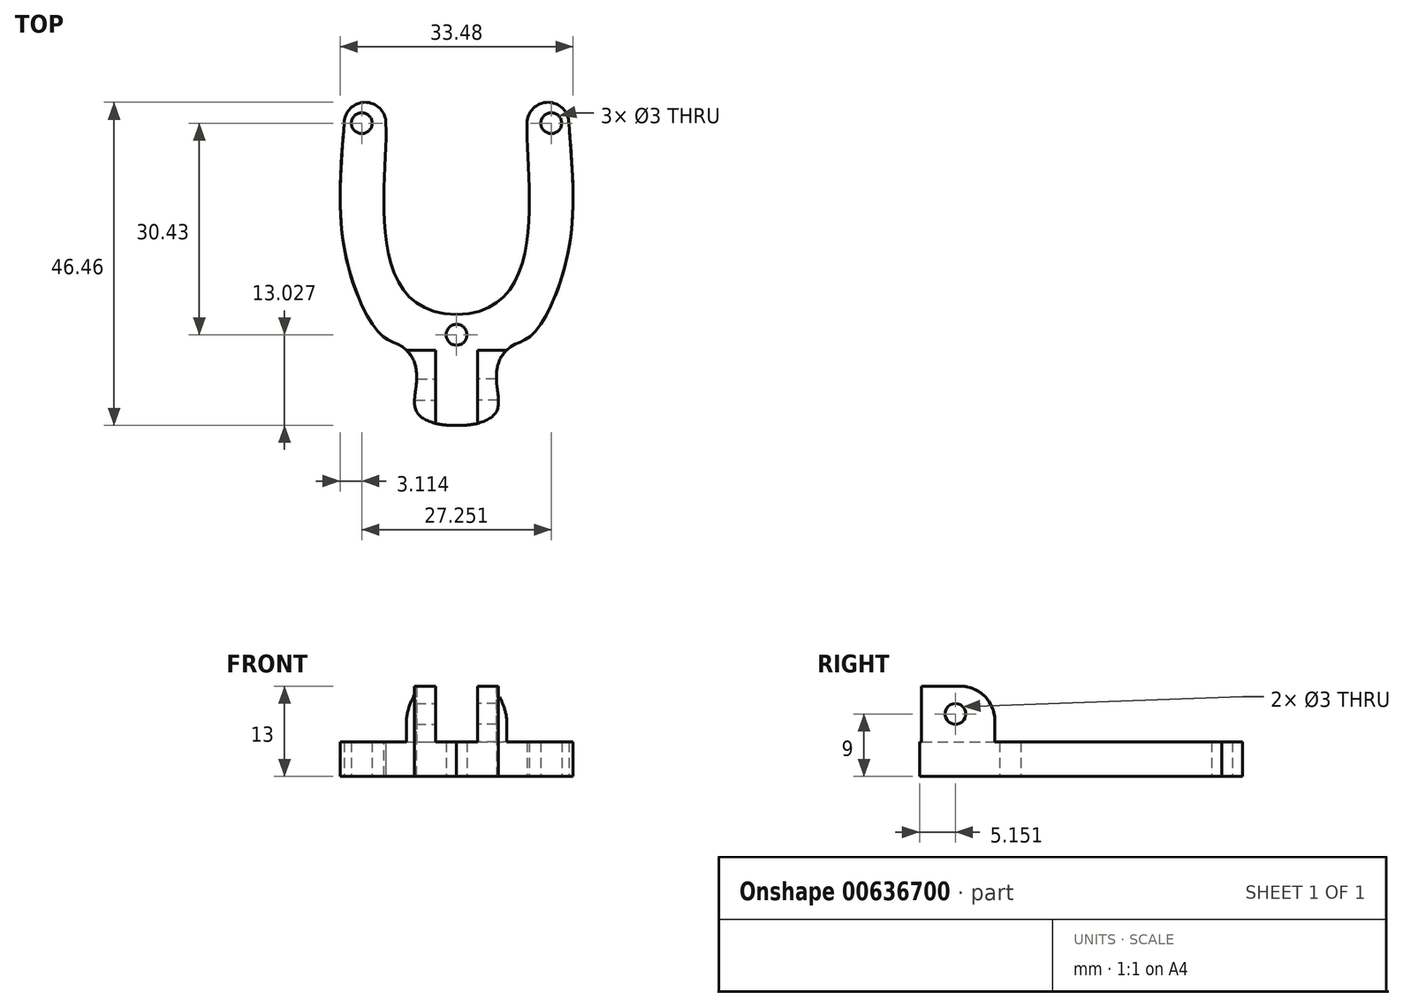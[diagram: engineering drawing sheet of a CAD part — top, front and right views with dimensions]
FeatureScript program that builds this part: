
annotation { "Feature Type Name" : "Feature", "Feature Type Description" : "" }
export const myFeature = defineFeature(function(context is Context, id is Id, definition is map)
    precondition{}
    {
        {
            var Q0;
            Q0=qCreatedBy(makeId("Top.planeOp"),FACE);
            var sketch = newSketch(context, id + "F0", { "sketchPlane" : qUnion([Q0])});
            skPoint(sketch, "E0.visualSharp", {"position": v(16.15, 56.7) * mm});
            skArc(sketch, "E0.filletArc", {"start": v(16.15, 51.7) * mm, "mid": v(15.24, 53.85) * mm, "end": v(13.06, 54.7) * mm});
            skPoint(sketch, "E1.visualSharp", {"position": v(8.63, 49.82) * mm});
            skPoint(sketch, "E2.visualSharp", {"position": v(8.63, 22.1) * mm});
            skCircle(sketch, "E3.MirrorC", {"center": v(13.63, 51.7) * mm, "radius": 1.5 * mm});
            skArc(sketch, "E4", {"start": v(13.06, 54.7) * mm, "mid": v(11, 53.79) * mm, "end": v(10.15, 51.7) * mm});
            skFitSpline(sketch, "E5", {"points": [v(10.15, 51.7) * mm, v(0, 24.2) * mm], "startDerivative": vector(-1.26, -21.95) * mm, "endDerivative": vector(-42.1, -0.2) * mm});
            skCircle(sketch, "E6.MirrorC", {"center": v(-13.63, 51.7) * mm, "radius": 1.5 * mm});
            skArc(sketch, "E7.MirrorCS", {"start": v(-16.15, 51.7) * mm, "mid": v(-15.24, 53.85) * mm, "end": v(-13.06, 54.7) * mm});
            skCircle(sketch, "E8.MirrorC", {"center": v(0, 21.27) * mm, "radius": 1.5 * mm});
            skArc(sketch, "E9.MirrorCS", {"start": v(-13.06, 54.7) * mm, "mid": v(-11, 53.79) * mm, "end": v(-10.15, 51.7) * mm});
            skPoint(sketch, "E10.MirrorP", {"position": v(-16.15, 56.7) * mm});
            skPoint(sketch, "E11.MirrorP", {"position": v(-8.63, 22.1) * mm});
            skFitSpline(sketch, "E12.MirrorCS", {"points": [v(-10.15, 51.7) * mm, v(0, 24.2) * mm], "startDerivative": vector(1.26, -21.95) * mm, "endDerivative": vector(42.1, -0.2) * mm});
            skPoint(sketch, "E13.MirrorP", {"position": v(-8.63, 49.82) * mm});
            skFitSpline(sketch, "E14", {"points": [v(-16.15, 51.7) * mm, v(-16.15, 33.71) * mm, v(-10.93, 21.33) * mm, v(-8.08, 19.72) * mm, v(-6.15, 17.52) * mm, v(-5.8, 13.9) * mm, v(-5.58, 9.97) * mm, v(0, 8.27) * mm], "startDerivative": vector(-5.54, -74.98) * mm, "endDerivative": vector(45.3, 3.48) * mm});
            skFitSpline(sketch, "E15.MirrorCS", {"points": [v(16.15, 51.7) * mm, v(16.15, 33.71) * mm, v(10.93, 21.33) * mm, v(8.08, 19.72) * mm, v(6.15, 17.52) * mm, v(5.8, 13.9) * mm, v(5.58, 9.97) * mm, v(0, 8.27) * mm], "startDerivative": vector(5.54, -74.98) * mm, "endDerivative": vector(-45.3, 3.48) * mm});
            skSolve(sketch);
        }
        {
            var Q0;
            Q0=makeQuery(id+"F0.imprint","IMPRINT",FACE,{"disambiguationData":[TD([[makeQuery(id+"F0.imprint","IMPRINT",EDGE,{"derivedFrom":sQuery(id+"F0.wireOp",EDGE,"E0.filletArc")}),1.0]])]});
            extrude(context, id + "F1", {"entities" : qUnion([Q0]), "depth" : 5 * mm, "offsetDistance" : 25 * mm});
        }
        {
            var Q0;
            Q0=makeQuery(id+"F1.opExtrude","CAP_FACE",FACE,{"disambiguationData":[OSD([sQuery(id+"F0.wireOp",EDGE,"E0.filletArc"),sQuery(id+"F0.wireOp",EDGE,"E3.MirrorC"),sQuery(id+"F0.wireOp",EDGE,"E4"),sQuery(id+"F0.wireOp",EDGE,"E5"),sQuery(id+"F0.wireOp",EDGE,"E6.MirrorC"),sQuery(id+"F0.wireOp",EDGE,"E7.MirrorCS"),sQuery(id+"F0.wireOp",EDGE,"E8.MirrorC"),sQuery(id+"F0.wireOp",EDGE,"E9.MirrorCS"),sQuery(id+"F0.wireOp",EDGE,"E12.MirrorCS"),sQuery(id+"F0.wireOp",EDGE,"E14"),sQuery(id+"F0.wireOp",EDGE,"E15.MirrorCS")])],"isStart":false});
            var sketch = newSketch(context, id + "F2", { "sketchPlane" : qUnion([Q0])});
            skPoint(sketch, "E16.visualSharp", {"position": v(16.15, 56.7) * mm});
            skArc(sketch, "E16.filletArc", {"start": v(16.15, 51.7) * mm, "mid": v(15.24, 53.84) * mm, "end": v(13.06, 54.7) * mm});
            skPoint(sketch, "E17.visualSharp", {"position": v(8.63, 49.8) * mm});
            skPoint(sketch, "E18.visualSharp", {"position": v(8.63, 22.1) * mm});
            skCircle(sketch, "E19.MirrorC", {"center": v(13.63, 51.7) * mm, "radius": 1.5 * mm});
            skArc(sketch, "E20", {"start": v(13.06, 54.7) * mm, "mid": v(11, 53.78) * mm, "end": v(10.15, 51.7) * mm});
            skFitSpline(sketch, "E21", {"points": [v(10.15, 51.7) * mm, v(0, 24.2) * mm], "startDerivative": vector(-1.26, -21.95) * mm, "endDerivative": vector(-42.1, -0.2) * mm});
            skCircle(sketch, "E22.MirrorC", {"center": v(-13.63, 51.7) * mm, "radius": 1.5 * mm});
            skArc(sketch, "E23.MirrorCS", {"start": v(-16.15, 51.7) * mm, "mid": v(-15.24, 53.84) * mm, "end": v(-13.06, 54.7) * mm});
            skCircle(sketch, "E24.MirrorC", {"center": v(0, 21.26) * mm, "radius": 1.5 * mm});
            skArc(sketch, "E25.MirrorCS", {"start": v(-13.06, 54.7) * mm, "mid": v(-11, 53.78) * mm, "end": v(-10.15, 51.7) * mm});
            skPoint(sketch, "E26.MirrorP", {"position": v(-16.15, 56.7) * mm});
            skPoint(sketch, "E27.MirrorP", {"position": v(-8.63, 22.1) * mm});
            skFitSpline(sketch, "E28.MirrorCS", {"points": [v(-10.15, 51.7) * mm, v(0, 24.2) * mm], "startDerivative": vector(1.26, -21.95) * mm, "endDerivative": vector(42.1, -0.2) * mm});
            skPoint(sketch, "E29.MirrorP", {"position": v(-8.63, 49.8) * mm});
            skFitSpline(sketch, "E30", {"points": [v(-16.15, 51.7) * mm, v(-16.15, 33.7) * mm, v(-10.93, 21.32) * mm, v(-8.08, 19.71) * mm, v(-6.15, 17.51) * mm, v(-5.8, 13.89) * mm, v(-5.58, 9.96) * mm, v(0, 8.26) * mm], "startDerivative": vector(-5.54, -74.98) * mm, "endDerivative": vector(45.3, 3.48) * mm});
            skFitSpline(sketch, "E31.MirrorCS", {"points": [v(16.15, 51.7) * mm, v(16.15, 33.7) * mm, v(10.93, 21.32) * mm, v(8.08, 19.71) * mm, v(6.15, 17.51) * mm, v(5.8, 13.89) * mm, v(5.58, 9.96) * mm, v(0, 8.26) * mm], "startDerivative": vector(5.54, -74.98) * mm, "endDerivative": vector(-45.3, 3.48) * mm});
            skLineSegment(sketch, "E32", {"start": v(-7.2, 19.05) * mm, "end": v(7.2, 19.05) * mm});
            skLineSegment(sketch, "E33.left", {"start": v(3, 8.52) * mm, "end": v(3, 19.05) * mm});
            skLineSegment(sketch, "E33.right", {"start": v(-3, 8.52) * mm, "end": v(-3, 19.05) * mm});
            skPoint(sketch, "E33.middle", {"position": v(0, 12.94) * mm});
            skPoint(sketch, "E34.orphan", {"position": v(-3, 19.47) * mm});
            skPoint(sketch, "E35.orphan", {"position": v(3, 19.47) * mm});
            skPoint(sketch, "E33.bottom.end.orphan", {"position": v(-3, 6.42) * mm});
            skPoint(sketch, "E33.bottom.start.orphan", {"position": v(3, 6.42) * mm});
            skSolve(sketch);
        }
        {
            var Q0;
            {var subQ0=sQuery(id+"F2.wireOp",EDGE,"E30");var subQ1=makeQuery(id+"F1.opExtrude","CAP_EDGE",EDGE,{"disambiguationData":[OSD([sQuery(id+"F0.wireOp",EDGE,"E14")])],"isStart":false});var subQ4=makeQuery(id+"F2.imprint","INTERSECT",VERTEX,{"disambiguationData":[OD(1.0)],"derivedFrom":[subQ1,subQ0]});var subQ8=makeQuery(id+"F2.imprint","IMPRINT",VERTEX,{"derivedFrom":subQ0});Q0=makeQuery(id+"F2.imprint","IMPRINT",FACE,{"disambiguationData":[TD([[makeQuery(id+"F2.imprint","IMPRINT",EDGE,{"disambiguationData":[TD([[subQ8,1.0],[subQ4,-1.0]]),OD(1.0)],"derivedFrom":subQ0}),1.0]])]});}
            var Q1;
            {var subQ0=sQuery(id+"F2.wireOp",EDGE,"E31.MirrorCS");var subQ1=makeQuery(id+"F1.opExtrude","CAP_EDGE",EDGE,{"disambiguationData":[OSD([sQuery(id+"F0.wireOp",EDGE,"E15.MirrorCS")])],"isStart":false});var subQ5=makeQuery(id+"F2.imprint","IMPRINT",VERTEX,{"derivedFrom":subQ0});var subQ10=makeQuery(id+"F2.imprint","INTERSECT",VERTEX,{"disambiguationData":[OD(1.0)],"derivedFrom":[subQ1,subQ0]});Q1=makeQuery(id+"F2.imprint","IMPRINT",FACE,{"disambiguationData":[TD([[makeQuery(id+"F2.imprint","IMPRINT",EDGE,{"disambiguationData":[TD([[subQ5,1.0],[subQ10,-1.0]]),OD(1.0)],"derivedFrom":subQ0}),-1.0]])]});}
            extrude(context, id + "F3", {"entities" : qUnion([Q0, Q1]), "operationType" : NewBodyOperationType.ADD, "depth" : 8 * mm, "offsetDistance" : 25 * mm});
        }
        {
            var Q0;
            {var subQ0=sQuery(id+"F2.wireOp",EDGE,"E32");Q0=makeQuery(id+"F3.opExtrude","CAP_EDGE",EDGE,{"disambiguationData":[OSD([subQ0]),TDD([makeQuery(id+"F2.imprint","IMPRINT",EDGE,{"disambiguationData":[TD([[makeQuery(id+"F2.imprint","INTERSECT",VERTEX,{"derivedFrom":[subQ0,sQuery(id+"F2.wireOp",EDGE,"E33.right")]}),1.0]])],"derivedFrom":subQ0})])],"isStart":false});}
            fillet(context, id + "F4", {"entities" : qUnion([Q0]), "radius" : 5 * mm, "tangentPropagation" : true, "allowEdgeOverflow" : false});
        }
        {
            var Q0;
            {var subQ0=sQuery(id+"F2.wireOp",EDGE,"E32");Q0=makeQuery(id+"F3.opExtrude","CAP_EDGE",EDGE,{"disambiguationData":[OSD([subQ0]),TDD([makeQuery(id+"F2.imprint","IMPRINT",EDGE,{"disambiguationData":[TD([[makeQuery(id+"F2.imprint","INTERSECT",VERTEX,{"derivedFrom":[subQ0,sQuery(id+"F2.wireOp",EDGE,"E33.left")]}),-1.0]])],"derivedFrom":subQ0})])],"isStart":false});}
            fillet(context, id + "F5", {"entities" : qUnion([Q0]), "radius" : 5 * mm, "tangentPropagation" : true, "allowEdgeOverflow" : false});
        }
        {
            var Q0;
            Q0=qCreatedBy(makeId("Right.planeOp"),FACE);
            var sketch = newSketch(context, id + "F6", { "sketchPlane" : qUnion([Q0])});
            skCircle(sketch, "E36", {"center": v(13.4, 9) * mm, "radius": 1.5 * mm});
            skSolve(sketch);
        }
        {
            var Q0;
            Q0=makeQuery(id+"F6.imprint","IMPRINT",FACE,{"disambiguationData":[TD([[makeQuery(id+"F6.imprint","IMPRINT",EDGE,{"derivedFrom":sQuery(id+"F6.wireOp",EDGE,"E36")}),1.0]])]});
            extrude(context, id + "F7", {"entities" : qUnion([Q0]), "operationType" : NewBodyOperationType.REMOVE, "oppositeDirection" : true, "depth" : 25 * mm, "offsetDistance" : 25 * mm});
        }
        {
            var Q0;
            Q0 = qSketchRegion(id + "F6", true);
            extrude(context, id + "F8", {"entities" : qUnion([Q0]), "operationType" : NewBodyOperationType.REMOVE, "depth" : 25 * mm, "offsetDistance" : 25 * mm});
        }
    });
